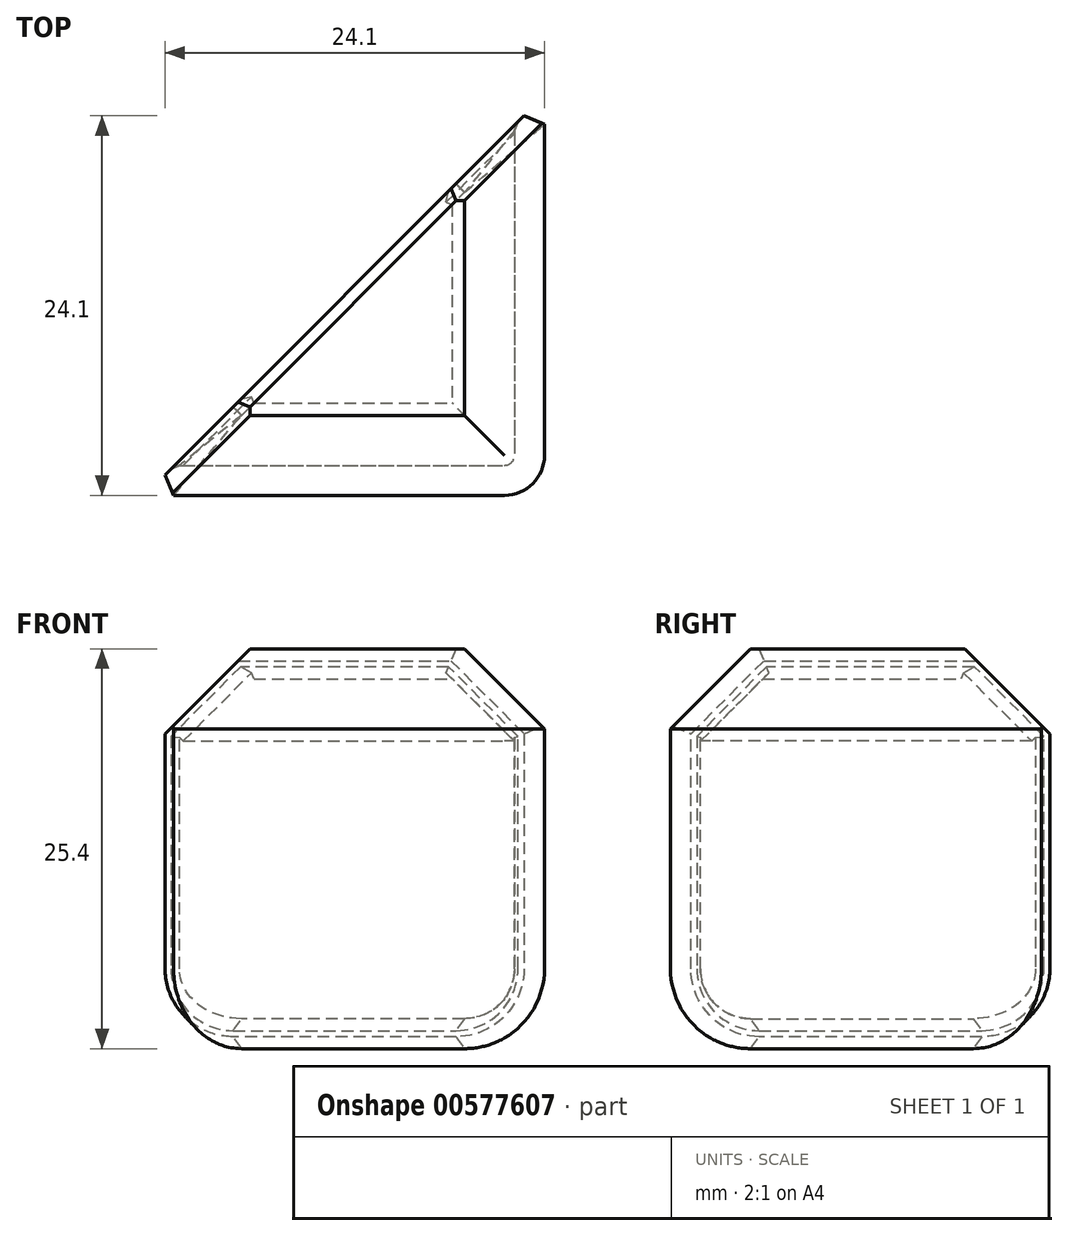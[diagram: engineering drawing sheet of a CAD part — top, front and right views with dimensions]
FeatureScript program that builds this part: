
annotation { "Feature Type Name" : "Feature", "Feature Type Description" : "" }
export const myFeature = defineFeature(function(context is Context, id is Id, definition is map)
    precondition{}
    {
        {
            var Q0;
            Q0=qCreatedBy(makeId("Top.planeOp"),FACE);
            var sketch = newSketch(context, id + "F0", { "sketchPlane" : qUnion([Q0])});
            skLineSegment(sketch, "E0.bottom", {"start": v(0, 0) * mm, "end": v(25.4, 0) * mm});
            skLineSegment(sketch, "E0.top", {"start": v(0, 25.4) * mm, "end": v(25.4, 25.4) * mm});
            skLineSegment(sketch, "E0.left", {"start": v(0, 0) * mm, "end": v(0, 25.4) * mm});
            skLineSegment(sketch, "E0.right", {"start": v(25.4, 0) * mm, "end": v(25.4, 25.4) * mm});
            skSolve(sketch);
        }
        {
            var Q0;
            Q0=makeQuery(id+"F0.imprint","IMPRINT",FACE,{"disambiguationData":[TD([[makeQuery(id+"F0.imprint","IMPRINT",EDGE,{"derivedFrom":sQuery(id+"F0.wireOp",EDGE,"E0.bottom")}),1.0]])]});
            extrude(context, id + "F1", {"entities" : qUnion([Q0]), "depth" : 25.4 * mm, "offsetDistance" : 25.4 * mm});
        }
        {
            var Q0;
            Q0=makeQuery(id+"F1.opExtrude","SWEPT_EDGE",EDGE,{"disambiguationData":[OSD([sQuery(id+"F0.wireOp",EDGE,"E0.bottom"),sQuery(id+"F0.wireOp",EDGE,"E0.right")])]});
            fillet(context, id + "F2", {"entities" : qUnion([Q0]), "radius" : 2.54 * mm, "tangentPropagation" : true, "allowEdgeOverflow" : false});
        }
        {
            var Q0;
            Q0=makeQuery(id+"F1.opExtrude","SWEPT_FACE",FACE,{"disambiguationData":[OSD([sQuery(id+"F0.wireOp",EDGE,"E0.left")])]});
            var sketch = newSketch(context, id + "F3", { "sketchPlane" : qUnion([Q0])});
            skLineSegment(sketch, "E1", {"start": v(0, 25.4) * mm, "end": v(0, 20.32) * mm});
            skLineSegment(sketch, "E2", {"start": v(0, 20.32) * mm, "end": v(-5.08, 25.4) * mm});
            skLineSegment(sketch, "E3", {"start": v(-5.08, 25.4) * mm, "end": v(0, 25.4) * mm});
            skSolve(sketch);
        }
        {
            var Q0;
            {var subQ4=sQuery(id+"F3.wireOp",EDGE,"E2");Q0=makeQuery(id+"F3.imprint","IMPRINT",FACE,{"disambiguationData":[TD([[makeQuery(id+"F3.imprint","IMPRINT",EDGE,{"derivedFrom":subQ4}),1.0]])]});}
            var sketch = newSketch(context, id + "F4", { "sketchPlane" : qUnion([Q0])});
            skLineSegment(sketch, "E4", {"start": v(0, 5.08) * mm, "end": v(0, 0) * mm});
            skLineSegment(sketch, "E5", {"start": v(0, 0) * mm, "end": v(-5.08, 0) * mm});
            skLineSegment(sketch, "E6", {"start": v(-5.08, 0) * mm, "end": v(0, 5.08) * mm, "construction": true});
            skArc(sketch, "E7", {"start": v(-5.08, 0) * mm, "mid": v(-1.49, 1.49) * mm, "end": v(0, 5.08) * mm});
            skSolve(sketch);
        }
        {
            var Q0;
            Q0=makeQuery(id+"F3.imprint","IMPRINT",FACE,{"disambiguationData":[TD([[makeQuery(id+"F3.imprint","IMPRINT",EDGE,{"derivedFrom":sQuery(id+"F3.wireOp",EDGE,"E1")}),-1.0]])]});
            var Q1;
            Q1=makeQuery(id+"F4.imprint","IMPRINT",FACE,{"disambiguationData":[TD([[makeQuery(id+"F4.imprint","IMPRINT",EDGE,{"derivedFrom":sQuery(id+"F4.wireOp",EDGE,"E4")}),-1.0]])]});
            var Q2;
            Q2=makeQuery(id+"F1.opExtrude","CAP_EDGE",EDGE,{"disambiguationData":[OSD([sQuery(id+"F0.wireOp",EDGE,"E0.bottom")])],"isStart":false});
            sweep(context, id + "F5", {"operationType" : NewBodyOperationType.REMOVE, "profiles" : qUnion([Q0, Q1]), "path" : qUnion([Q2])});
        }
        {
            var Q0;
            Q0=makeQuery(id+"F1.opExtrude","SWEPT_FACE",FACE,{"disambiguationData":[OSD([sQuery(id+"F0.wireOp",EDGE,"E0.top")])]});
            var sketch = newSketch(context, id + "F6", { "sketchPlane" : qUnion([Q0])});
            skLineSegment(sketch, "E8", {"start": v(-25.4, 25.4) * mm, "end": v(-20.32, 25.4) * mm});
            skLineSegment(sketch, "E9", {"start": v(-20.32, 25.4) * mm, "end": v(-25.4, 20.32) * mm});
            skLineSegment(sketch, "E10", {"start": v(-25.4, 20.32) * mm, "end": v(-25.4, 25.4) * mm});
            skSolve(sketch);
        }
        {
            var Q0;
            Q0=makeQuery(id+"F1.opExtrude","SWEPT_FACE",FACE,{"disambiguationData":[OSD([sQuery(id+"F0.wireOp",EDGE,"E0.top")])]});
            var sketch = newSketch(context, id + "F7", { "sketchPlane" : qUnion([Q0])});
            skLineSegment(sketch, "E11", {"start": v(-20.32, 0) * mm, "end": v(-25.4, 0) * mm});
            skLineSegment(sketch, "E12", {"start": v(-25.4, 0) * mm, "end": v(-25.4, 5.08) * mm});
            skLineSegment(sketch, "E13", {"start": v(-25.4, 5.08) * mm, "end": v(-20.32, 0) * mm, "construction": true});
            skArc(sketch, "E14", {"start": v(-25.4, 5.08) * mm, "mid": v(-23.91, 1.49) * mm, "end": v(-20.32, 0) * mm});
            skSolve(sketch);
        }
        {
            var Q0;
            Q0=makeQuery(id+"F6.imprint","IMPRINT",FACE,{"disambiguationData":[TD([[makeQuery(id+"F6.imprint","IMPRINT",EDGE,{"derivedFrom":sQuery(id+"F6.wireOp",EDGE,"E8")}),1.0]])]});
            var Q1;
            Q1=makeQuery(id+"F7.imprint","IMPRINT",FACE,{"disambiguationData":[TD([[makeQuery(id+"F7.imprint","IMPRINT",EDGE,{"derivedFrom":sQuery(id+"F7.wireOp",EDGE,"E11")}),-1.0]])]});
            var Q2;
            Q2=makeQuery(id+"F1.opExtrude","CAP_EDGE",EDGE,{"disambiguationData":[OSD([sQuery(id+"F0.wireOp",EDGE,"E0.right")])],"isStart":false});
            sweep(context, id + "F8", {"operationType" : NewBodyOperationType.REMOVE, "profiles" : qUnion([Q0, Q1]), "path" : qUnion([Q2])});
        }
        {
            var Q0;
            Q0=makeQuery(id+"F5.boolean.opBoolean","COPY",FACE,{"derivedFrom":makeQuery(id+"F5.opSweep","CAP_FACE",FACE,{"disambiguationData":[OSD([sQuery(id+"F0.wireOp",EDGE,"E0.bottom"),sQuery(id+"F0.wireOp",EDGE,"E0.top"),sQuery(id+"F0.wireOp",EDGE,"E0.left"),sQuery(id+"F0.wireOp",EDGE,"E0.right"),sQuery(id+"F3.wireOp",EDGE,"E1"),sQuery(id+"F3.wireOp",EDGE,"E2"),sQuery(id+"F3.wireOp",EDGE,"E3")])],"isStart":false})});
            var Q1;
            Q1=makeQuery(id+"F5.boolean.opBoolean","COPY",FACE,{"derivedFrom":makeQuery(id+"F5.opSweep","CAP_FACE",FACE,{"disambiguationData":[OSD([sQuery(id+"F0.wireOp",EDGE,"E0.bottom"),sQuery(id+"F0.wireOp",EDGE,"E0.top"),sQuery(id+"F0.wireOp",EDGE,"E0.left"),sQuery(id+"F0.wireOp",EDGE,"E0.right"),sQuery(id+"F4.wireOp",EDGE,"E4"),sQuery(id+"F4.wireOp",EDGE,"E5"),sQuery(id+"F4.wireOp",EDGE,"E7")])],"isStart":false})});
            var Q2;
            {var subQ0=sQuery(id+"F0.wireOp",EDGE,"E0.right");var subQ1=sQuery(id+"F0.wireOp",EDGE,"E0.bottom");Q2=makeQuery(id+"F2.opFillet","BLEND_EDGE",EDGE,{"blendedFrom":[makeQuery(id+"F1.opExtrude","SWEPT_EDGE",EDGE,{"disambiguationData":[OSD([subQ1,subQ0])]}),makeQuery(id+"F1.opExtrude","CAP_FACE",FACE,{"disambiguationData":[OSD([subQ1,sQuery(id+"F0.wireOp",EDGE,"E0.top"),sQuery(id+"F0.wireOp",EDGE,"E0.left"),subQ0])],"isStart":false})],"blendedInto":[makeQuery(id+"F1.opExtrude","CAP_FACE",FACE,{"disambiguationData":[OSD([subQ1,sQuery(id+"F0.wireOp",EDGE,"E0.top"),sQuery(id+"F0.wireOp",EDGE,"E0.left"),subQ0])],"isStart":false})]});}
            sweep(context, id + "F9", {"operationType" : NewBodyOperationType.REMOVE, "profiles" : qUnion([Q0, Q1]), "path" : qUnion([Q2])});
        }
        {
            var Q0;
            {var subQ0=sQuery(id+"F0.wireOp",EDGE,"E0.top");var subQ1=sQuery(id+"F0.wireOp",EDGE,"E0.left");var subQ2=sQuery(id+"F0.wireOp",EDGE,"E0.bottom");var subQ3=sQuery(id+"F0.wireOp",EDGE,"E0.right");Q0=makeQuery(id+"F8.boolean.opBoolean","SPLIT",FACE,{"disambiguationData":[TD([makeQuery(id+"F1.opExtrude","SWEPT_FACE",FACE,{"disambiguationData":[OSD([subQ0])]})])],"derivedFrom":makeQuery(id+"F1.opExtrude","CAP_FACE",FACE,{"disambiguationData":[OSD([subQ2,subQ0,subQ1,subQ3])],"isStart":true})});}
            var sketch = newSketch(context, id + "F10", { "sketchPlane" : qUnion([Q0])});
            skLineSegment(sketch, "E15", {"start": v(0, -25.4) * mm, "end": v(25.4, -25.4) * mm});
            skLineSegment(sketch, "E16", {"start": v(25.4, -25.4) * mm, "end": v(0, 0) * mm});
            skLineSegment(sketch, "E17", {"start": v(0, 0) * mm, "end": v(0, -25.4) * mm});
            skSolve(sketch);
        }
        {
            var Q0;
            Q0 = qSketchRegion(id + "F10", true);
            extrude(context, id + "F11", {"entities" : qUnion([Q0]), "operationType" : NewBodyOperationType.REMOVE, "endBound" : BoundingType.THROUGH_ALL, "oppositeDirection" : true, "depth" : 25.4 * mm, "offsetDistance" : 25.4 * mm});
        }
        {
            var Q0;
            Q0=makeQuery(id+"F11.boolean.opBoolean","COPY",FACE,{"derivedFrom":makeQuery(id+"F11.opExtrude","SWEPT_FACE",FACE,{"disambiguationData":[OSD([sQuery(id+"F10.wireOp",EDGE,"E16")])]})});
            shell(context, id + "F12", {"entities" : qUnion([Q0]), "thickness" : 1.9 * mm});
        }
        {
            var Q0;
            Q0=makeQuery(id+"F11.boolean.opBoolean","COPY",FACE,{"derivedFrom":makeQuery(id+"F11.opExtrude","SWEPT_FACE",FACE,{"disambiguationData":[OSD([sQuery(id+"F10.wireOp",EDGE,"E16")])]})});
            chamfer(context, id + "F13", {"entities" : qUnion([Q0]), "width" : 0.76 * mm, "tangentPropagation" : true});
        }
    });
